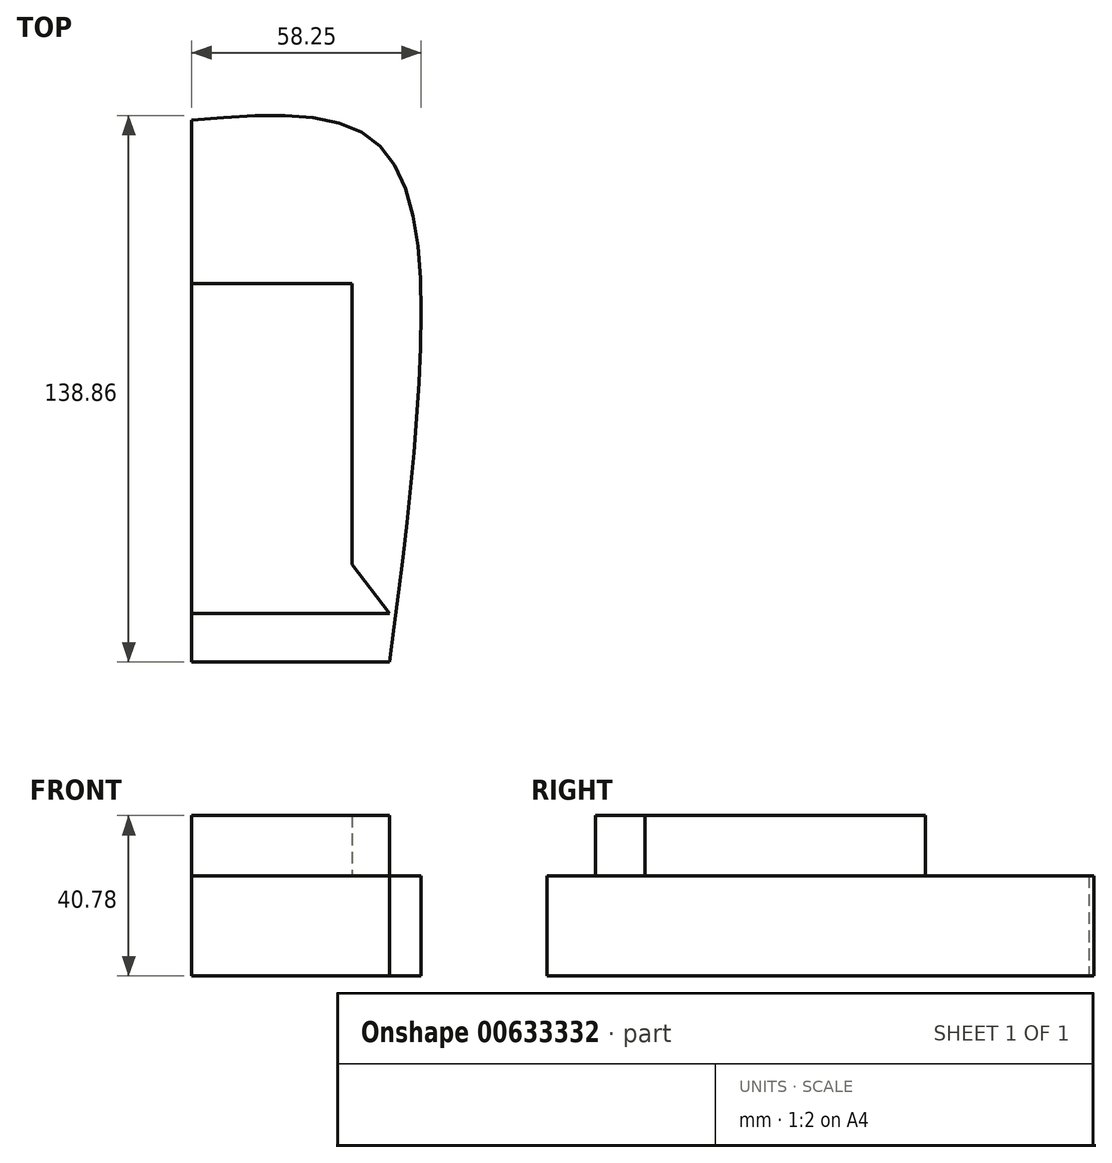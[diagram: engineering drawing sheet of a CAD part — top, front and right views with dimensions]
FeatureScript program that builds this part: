
annotation { "Feature Type Name" : "Feature", "Feature Type Description" : "" }
export const myFeature = defineFeature(function(context is Context, id is Id, definition is map)
    precondition{}
    {
        {
            var Q0;
            Q0=qCreatedBy(makeId("Top.planeOp"),FACE);
            var sketch = newSketch(context, id + "F0", { "sketchPlane" : qUnion([Q0])});
            skFitSpline(sketch, "E0", {"points": [v(0, 59.6) * mm, v(47.2, 53.54) * mm, v(58.03, 0) * mm, v(50.24, -78.11) * mm], "startDerivative": vector(187.16, 15.32) * mm, "endDerivative": vector(-26.76, -203.6) * mm});
            skLineSegment(sketch, "E1", {"start": v(50.24, -78.11) * mm, "end": v(0, -78.11) * mm});
            skLineSegment(sketch, "E2", {"start": v(0, -78.11) * mm, "end": v(0, 59.6) * mm});
            skSolve(sketch);
        }
        {
            var Q0;
            Q0=makeQuery(id+"F0.imprint","IMPRINT",FACE,{"disambiguationData":[TD([[makeQuery(id+"F0.imprint","IMPRINT",EDGE,{"derivedFrom":sQuery(id+"F0.wireOp",EDGE,"E0")}),-1.0]])]});
            var Q1;
            Q1 = qSketchRegion(id + "F0", true);
            extrude(context, id + "F1", {"entities" : qUnion([Q0, Q1]), "depth" : 25.4 * mm, "offsetDistance" : 25.4 * mm});
        }
        {
            var Q0;
            Q0=makeQuery(id+"F1.opExtrude","CAP_FACE",FACE,{"disambiguationData":[OSD([sQuery(id+"F0.wireOp",EDGE,"E0"),sQuery(id+"F0.wireOp",EDGE,"E1"),sQuery(id+"F0.wireOp",EDGE,"E2")])],"isStart":false});
            var sketch = newSketch(context, id + "F2", { "sketchPlane" : qUnion([Q0])});
            skLineSegment(sketch, "E3", {"start": v(0.3, -53.27) * mm, "end": v(40.76, -53.27) * mm});
            skLineSegment(sketch, "E4", {"start": v(40.76, -53.27) * mm, "end": v(40.76, 17.99) * mm});
            skLineSegment(sketch, "E5", {"start": v(40.76, 17.99) * mm, "end": v(0, 17.99) * mm});
            skLineSegment(sketch, "E6", {"start": v(0, 30.35) * mm, "end": v(40.76, 30.35) * mm});
            skLineSegment(sketch, "E7", {"start": v(40.76, 30.35) * mm, "end": v(40.76, 17.99) * mm});
            skLineSegment(sketch, "E8", {"start": v(0, -65.78) * mm, "end": v(50.24, -65.78) * mm});
            skLineSegment(sketch, "E9", {"start": v(50.24, -65.78) * mm, "end": v(40.76, 30.35) * mm});
            skLineSegment(sketch, "E10", {"start": v(40.76, -53.27) * mm, "end": v(50.24, -65.78) * mm});
            skSolve(sketch);
        }
        {
            var Q0;
            Q0=makeQuery(id+"F2.imprint","IMPRINT",FACE,{"disambiguationData":[TD([[makeQuery(id+"F2.imprint","IMPRINT",EDGE,{"derivedFrom":sQuery(id+"F2.wireOp",EDGE,"E4")}),1.0]])]});
            extrude(context, id + "F3", {"entities" : qUnion([Q0]), "operationType" : NewBodyOperationType.ADD, "depth" : 15.38 * mm, "offsetDistance" : 25.4 * mm});
        }
    });
